# Revit family: Overhead-Doors_Amarr_2743
name_source: partatom
category: Doors
units: mm (PartAtom-declared; Revit-internal decimal feet)

## family parameters
Always vertical = Yes
Classification Number = 23.30.10.17.37
Cut with Voids When Loaded = No
Host = Wall
Room Calculation Point = No
Shared = No

## types (1)
- Default - Load Type Catalog
    Analytic Construction = <None>
    Assembly Code = B2030410
    Description = Insulated Sectional Overhead Door
    Finish = Metal-Steel-Amarr_Entrematic-Paint-True_White
    Function = Exterior
    Glass = Glass-Amarr_Entrematic-Clear
    Heat Transfer Coefficient (U) = 0.1 BTU/(h·ft²·°F)
    Height = 7' - 0"
    Manufacturer = Amarr Entrematic
    Model = Amarr 2743
    Number of Hinges = 3
    Number of Windows = 2
    Operation = Sectional Overhead
    Panel - 1 = Yes
    Panel - 10 = No
    Panel - 11 = No
    Panel - 12 = No
    Panel - 13 = No
    Panel - 2 = Yes
    Panel - 4 = Yes
    Panel - 5 = No
    Panel - 6 = No
    Panel - 7 = No
    Panel - 8 = No
    Panel - 9 = No
    Panel 1 - 24 Inch = No
    Panel 10 - 24 Inch = No
    Panel 11 - 24 Inch = No
    Panel 12 - 24 Inch = No
    Panel 13 - 24 Inch = No
    Panel 2 - 24 Inch = No
    Panel 3 - 24 Inch = No
    Panel 4 - 24 Inch = No
    Panel 5 - 24 Inch = No
    Panel 6 - 24 Inch = No
    Panel 7 - 24 Inch = No
    Panel 8 - 24 Inch = No
    Panel 9 - 24 Inch = No
    Panel Window = 4' - 1"
    Product Documentation Link = http://www.amarr.com
    Product Name = Sectional Steel Door
    Product Page URL = http://www.amarr.com
    Rough Height = 7' - 0"
    Rough Width = 8' - 4"
    Solar Heat Gain Coefficient = 0
    Specification = http://www.amarr.com
    Thermal Resistance (R) = 10.0000 (h·ft²·°F)/BTU
    Thickness = 0' - 3"
    Torsion Bar Offset = 0' - 0"
    Track Height = 7' - 9 1/2"
    Track Offset = 0' - 3"
    Type Comments = 3 Inch Energy Efficient Super-Duty Polyurethane Insulated
    URL = http://www.amarr.com
    Visual Light Transmittance = 0
    Wall Closure = Interior
    Width = 8' - 2"
    Window Panel Offset = 3' - 6"
    Window Trim = Trim-Amarr_Entrematic-White

## geometry (parser evidence)
native form markers: Sweep x13
no freeform markers — native parametric forms only
